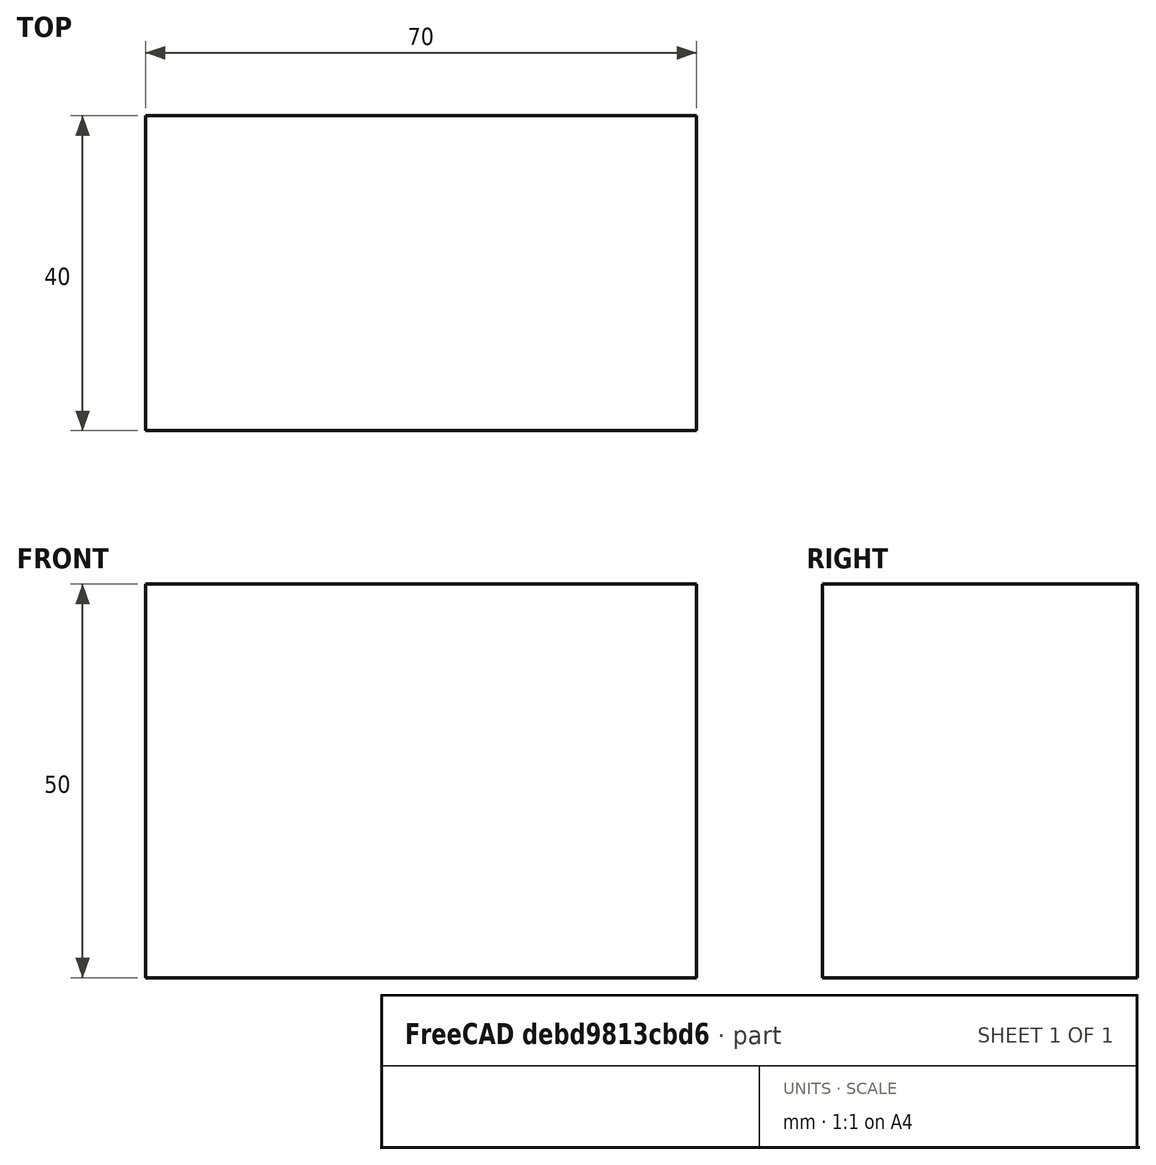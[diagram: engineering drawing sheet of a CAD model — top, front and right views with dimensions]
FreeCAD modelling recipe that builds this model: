
FCSTD DOCUMENT  (FreeCAD 0.15R4671 (Git))
Label: Flat Bar 70x40 EN10058 S235JR
License: All rights reserved
LicenseURL: http://en.wikipedia.org/wiki/All_rights_reserved
objects: Sketcher::SketchObject×1, Part::Extrusion×1
note: 2 computed .brp shape members not serialized (recipe doc carries the construction recipe); baked Part::Feature solids carry a one-line shape summary decoded from their .brp

FEATURE [Sketcher::SketchObject] Sketch
  sketch-geometry (4):
    g0: LineSegment StartX=-35 StartY=-20 StartZ=0 EndX=35 EndY=-20 EndZ=0
    g1: LineSegment StartX=35 StartY=-20 StartZ=0 EndX=35 EndY=20 EndZ=0
    g2: LineSegment StartX=35 StartY=20 StartZ=0 EndX=-35 EndY=20 EndZ=0
    g3: LineSegment StartX=-35 StartY=20 StartZ=0 EndX=-35 EndY=-20 EndZ=0
  constraints (12):
    c: Coincident(g0,g1)
    c: Coincident(g1,g2)
    c: Coincident(g2,g3)
    c: Coincident(g3,g0)
    c: Horizontal(g0)
    c: Horizontal(g2)
    c: Vertical(g1)
    c: Vertical(g3)
    c: Symmetric(g1,g2,g-2)
    c: Symmetric(g0,g1,g-1)
    c: DistanceY(g1) = 40
    c: DistanceX(g0) = 70
FEATURE [Part::Extrusion] Extrude  label="Flat Bar 70x40 EN10058 S235JR"
  Base = -> Sketch
  Dir = (0,0,50)
  Solid = true
